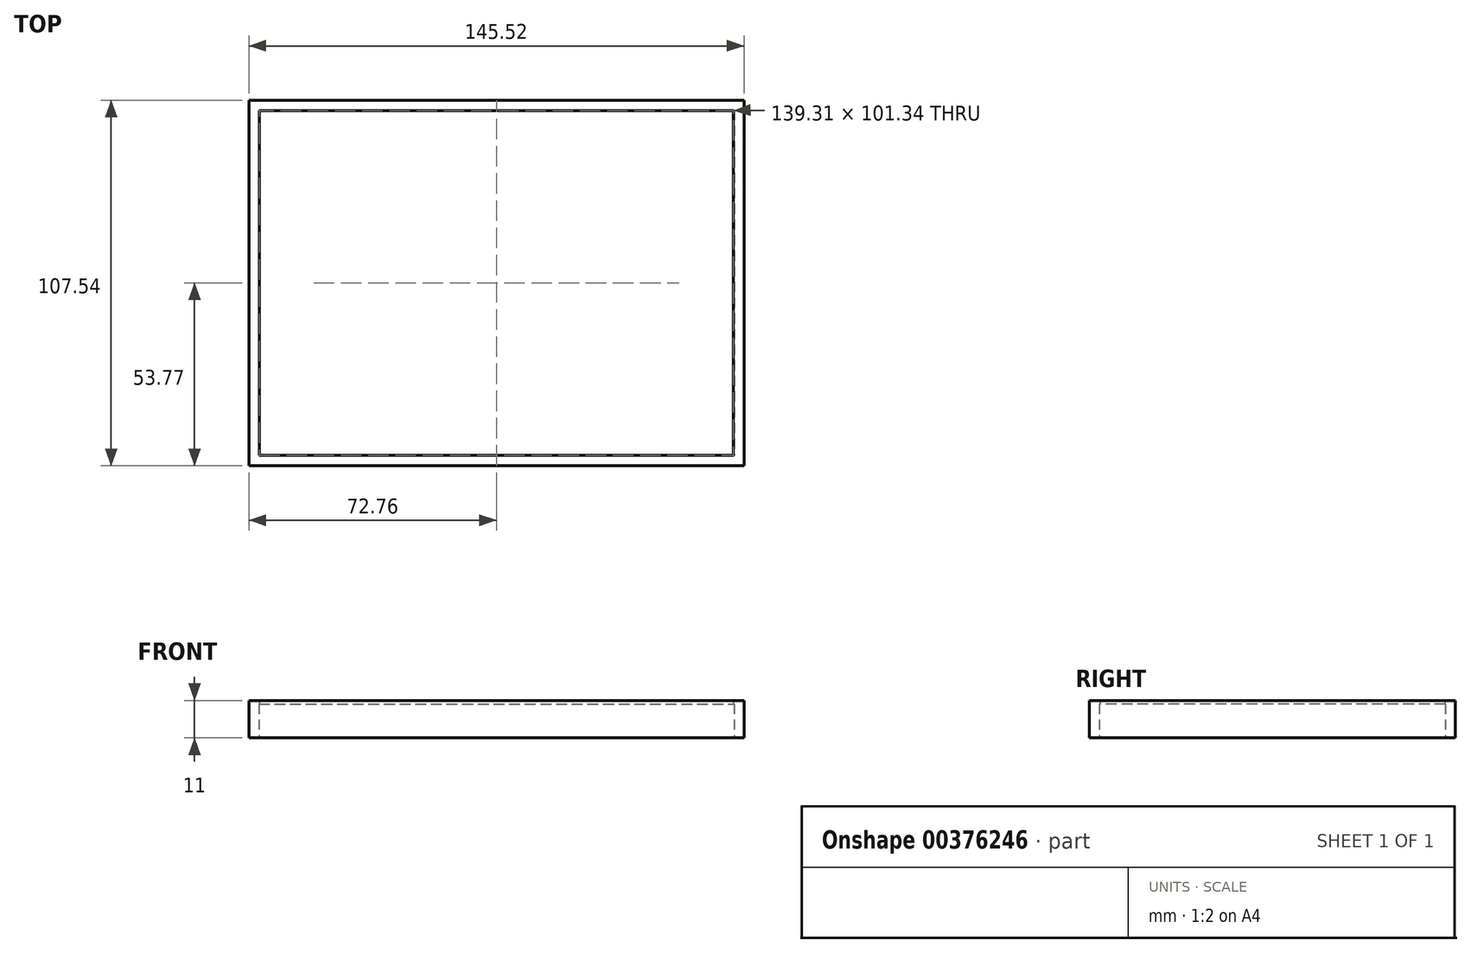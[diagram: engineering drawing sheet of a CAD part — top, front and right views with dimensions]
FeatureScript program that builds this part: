
annotation { "Feature Type Name" : "Feature", "Feature Type Description" : "" }
export const myFeature = defineFeature(function(context is Context, id is Id, definition is map)
    precondition{}
    {
        {
            var Q0;
            Q0=qCreatedBy(makeId("Top.planeOp"),FACE);
            var sketch = newSketch(context, id + "F0", { "sketchPlane" : qUnion([Q0])});
            skLineSegment(sketch, "E0.0", {"start": v(-69.66, 50.77) * mm, "end": v(-69.66, -50.77) * mm});
            skLineSegment(sketch, "E1.0", {"start": v(-69.76, 50.67) * mm, "end": v(69.76, 50.67) * mm});
            skLineSegment(sketch, "E2.0", {"start": v(69.66, 50.77) * mm, "end": v(69.66, -50.77) * mm});
            skLineSegment(sketch, "E3.0", {"start": v(-69.76, -50.67) * mm, "end": v(69.76, -50.67) * mm});
            skLineSegment(sketch, "E4.0", {"start": v(-72.76, 53.77) * mm, "end": v(-72.76, -53.77) * mm});
            skLineSegment(sketch, "E4.1", {"start": v(72.76, 53.77) * mm, "end": v(-72.76, 53.77) * mm});
            skLineSegment(sketch, "E4.2", {"start": v(72.76, -53.77) * mm, "end": v(72.76, 53.77) * mm});
            skLineSegment(sketch, "E4.3", {"start": v(-72.76, -53.77) * mm, "end": v(72.76, -53.77) * mm});
            skSolve(sketch);
        }
        {
            var Q0;
            Q0=makeQuery(id+"F0.imprint","IMPRINT",FACE,{"disambiguationData":[TD([[makeQuery(id+"F0.imprint","IMPRINT",EDGE,{"derivedFrom":sQuery(id+"F0.wireOp",EDGE,"E0.0")}),-1.0]])]});
            extrude(context, id + "F1", {"entities" : qUnion([Q0]), "depth" : 11 * mm, "offsetDistance" : 25 * mm});
        }
        {
            var Q0;
            Q0=qCreatedBy(makeId("Top.planeOp"),FACE);
            var sketch = newSketch(context, id + "F2", { "sketchPlane" : qUnion([Q0])});
            skLineSegment(sketch, "E5.0", {"start": v(-69.66, 50.67) * mm, "end": v(69.66, 50.67) * mm});
            skLineSegment(sketch, "E6.0", {"start": v(-69.66, 50.67) * mm, "end": v(-69.66, -50.67) * mm});
            skLineSegment(sketch, "E7.0", {"start": v(69.66, 50.67) * mm, "end": v(69.66, -50.67) * mm});
            skLineSegment(sketch, "E8.0", {"start": v(-69.66, -50.67) * mm, "end": v(69.66, -50.67) * mm});
            skLineSegment(sketch, "E9.0.0", {"start": v(-72.76, 53.77) * mm, "end": v(-72.76, -53.77) * mm});
            skLineSegment(sketch, "E9.0.1", {"start": v(-72.76, -53.77) * mm, "end": v(72.76, -53.77) * mm});
            skLineSegment(sketch, "E9.0.2", {"start": v(72.76, -53.77) * mm, "end": v(72.76, 53.77) * mm});
            skLineSegment(sketch, "E9.0.3", {"start": v(72.76, 53.77) * mm, "end": v(-72.76, 53.77) * mm});
            skLineSegment(sketch, "E10.0", {"start": v(-69.86, 50.87) * mm, "end": v(69.86, 50.87) * mm});
            skLineSegment(sketch, "E10.1", {"start": v(-69.86, 50.87) * mm, "end": v(-69.86, -50.87) * mm});
            skLineSegment(sketch, "E10.2", {"start": v(-69.86, -50.87) * mm, "end": v(69.86, -50.87) * mm});
            skLineSegment(sketch, "E10.3", {"start": v(69.86, 50.87) * mm, "end": v(69.86, -50.87) * mm});
            skSolve(sketch);
        }
        {
            var Q0;
            Q0=makeQuery(id+"F2.imprint","IMPRINT",FACE,{"disambiguationData":[TD([[makeQuery(id+"F2.imprint","IMPRINT",EDGE,{"derivedFrom":sQuery(id+"F2.wireOp",EDGE,"E5.0")}),1.0]])]});
            extrude(context, id + "F3", {"entities" : qUnion([Q0]), "operationType" : NewBodyOperationType.REMOVE, "depth" : 10 * mm, "offsetDistance" : 25 * mm});
        }
    });
